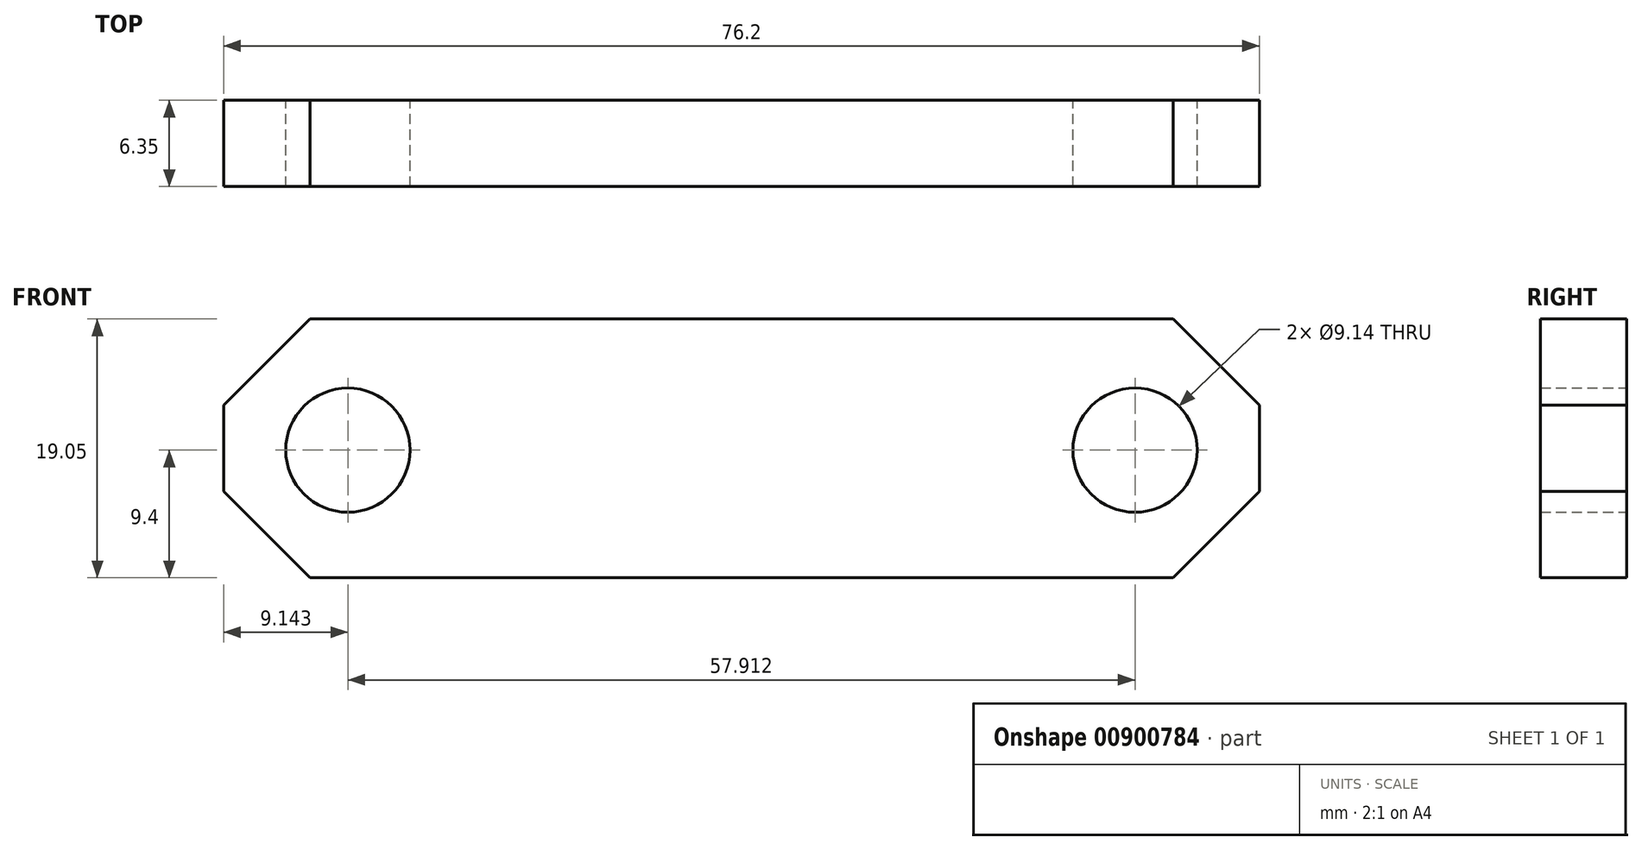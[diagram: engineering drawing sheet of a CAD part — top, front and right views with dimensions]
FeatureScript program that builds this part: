
annotation { "Feature Type Name" : "Feature", "Feature Type Description" : "" }
export const myFeature = defineFeature(function(context is Context, id is Id, definition is map)
    precondition{}
    {
        {
            var Q0;
            Q0=qCreatedBy(makeId("Front.planeOp"),FACE);
            var sketch = newSketch(context, id + "F0", { "sketchPlane" : qUnion([Q0])});
            skLineSegment(sketch, "E0.bottom", {"start": v(-30.94, 9.65) * mm, "end": v(45.26, 9.65) * mm});
            skLineSegment(sketch, "E0.top", {"start": v(-30.94, -9.4) * mm, "end": v(45.26, -9.4) * mm});
            skLineSegment(sketch, "E0.left", {"start": v(-30.94, 9.65) * mm, "end": v(-30.94, -9.4) * mm});
            skLineSegment(sketch, "E0.right", {"start": v(45.26, 9.65) * mm, "end": v(45.26, -9.4) * mm});
            skCircle(sketch, "E1", {"center": v(-21.8, 0) * mm, "radius": 4.57 * mm});
            skPoint(sketch, "E2.center.orphan", {"position": v(-8.34, 0) * mm});
            skPoint(sketch, "E2.end.orphan", {"position": v(-8.34, -4.57) * mm});
            skPoint(sketch, "E2.start.orphan", {"position": v(-8.34, 4.57) * mm});
            skPoint(sketch, "E3.center.orphan", {"position": v(36.11, 0) * mm});
            skPoint(sketch, "E3.end.orphan", {"position": v(36.11, 4.57) * mm});
            skCircle(sketch, "E4", {"center": v(36.11, 0) * mm, "radius": 4.57 * mm});
            skSolve(sketch);
        }
        {
            var Q0;
            Q0=makeQuery(id+"F0.imprint","IMPRINT",FACE,{"disambiguationData":[TD([[makeQuery(id+"F0.imprint","IMPRINT",EDGE,{"derivedFrom":sQuery(id+"F0.wireOp",EDGE,"E0.bottom")}),-1.0]])]});
            extrude(context, id + "F1", {"entities" : qUnion([Q0]), "depth" : 6.35 * mm, "offsetDistance" : 25.4 * mm});
        }
        {
            var Q0;
            Q0=makeQuery(id+"F1.opExtrude","SWEPT_EDGE",EDGE,{"disambiguationData":[OSD([sQuery(id+"F0.wireOp",EDGE,"E0.bottom"),sQuery(id+"F0.wireOp",EDGE,"E0.left")])]});
            var Q1;
            Q1=makeQuery(id+"F1.opExtrude","SWEPT_EDGE",EDGE,{"disambiguationData":[OSD([sQuery(id+"F0.wireOp",EDGE,"E0.bottom"),sQuery(id+"F0.wireOp",EDGE,"E0.right")])]});
            var Q2;
            Q2=makeQuery(id+"F1.opExtrude","SWEPT_EDGE",EDGE,{"disambiguationData":[OSD([sQuery(id+"F0.wireOp",EDGE,"E0.top"),sQuery(id+"F0.wireOp",EDGE,"E0.right")])]});
            chamfer(context, id + "F2", {"entities" : qUnion([Q0, Q1, Q2]), "width" : 6.35 * mm, "tangentPropagation" : true});
        }
        {
            var Q0;
            Q0=makeQuery(id+"F1.opExtrude","SWEPT_EDGE",EDGE,{"disambiguationData":[OSD([sQuery(id+"F0.wireOp",EDGE,"E0.top"),sQuery(id+"F0.wireOp",EDGE,"E0.left")])]});
            chamfer(context, id + "F3", {"entities" : qUnion([Q0]), "width" : 6.35 * mm, "tangentPropagation" : true});
        }
    });
